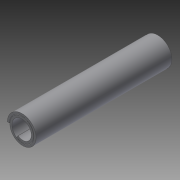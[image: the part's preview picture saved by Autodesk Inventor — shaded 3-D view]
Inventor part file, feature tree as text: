
AUTODESK INVENTOR PART (.ipt)
format: ipt  version: 2014 SP1 (Build 180222100, 222)  size: 119,808 bytes
history: native  units: in
note: dims shown in document units (in); Inventor stores cm internally (conversion verified against a paired STEP export)
features: sketch x4, other x2, sweep x1
ambient origin geometry x8: Origin, YZ Plane, XZ Plane, XY Plane, X Axis, Y Axis, Z Axis, Center Point
bodies: Solid1 (feature_tree)
feature tree (7):
  sketch  "Sketch1"  dims[d0=0.0085in d1=0.552in d2=0.122in d3=0.3in d4=0.552in d5=0.104in d6=-0.0137in d7=0.0in]
  sketch  "3D Sketch1"
  sketch  "3D Sketch2"
  sweep  "Sweep1"
  other  "Helical Curve1"
  sketch  "3D Sketch3"
  other  "Project to Surface1"
